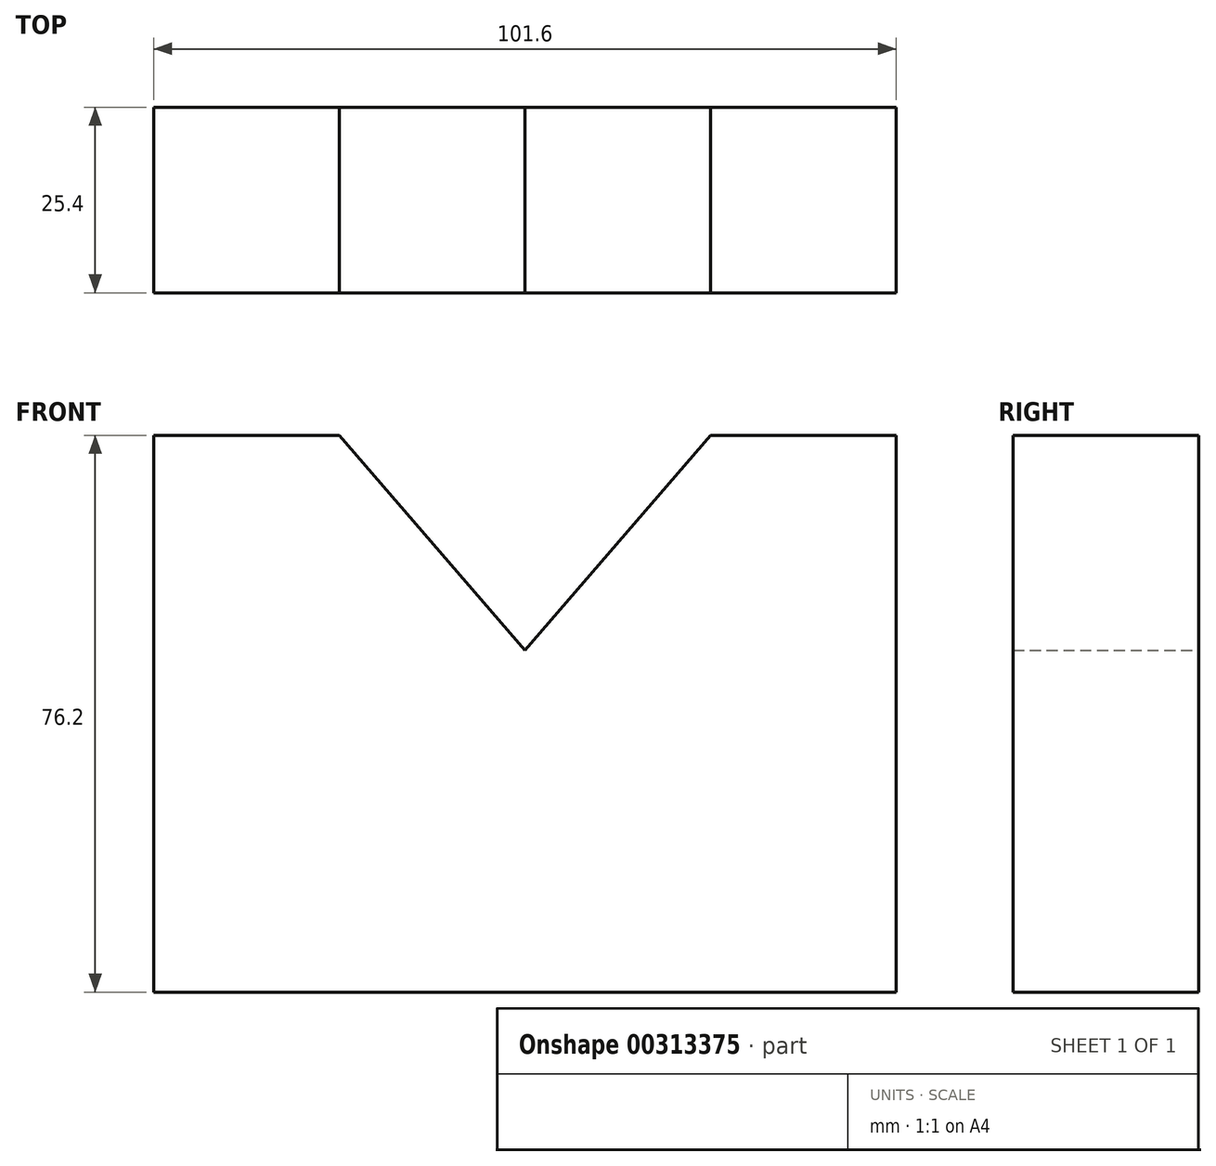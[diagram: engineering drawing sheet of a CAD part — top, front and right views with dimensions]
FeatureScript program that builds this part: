
annotation { "Feature Type Name" : "Feature", "Feature Type Description" : "" }
export const myFeature = defineFeature(function(context is Context, id is Id, definition is map)
    precondition{}
    {
        {
            var Q0;
            Q0=qCreatedBy(makeId("Front.planeOp"),FACE);
            var sketch = newSketch(context, id + "F0", { "sketchPlane" : qUnion([Q0])});
            skLineSegment(sketch, "E0", {"start": v(-43.63, -46.75) * mm, "end": v(57.97, -46.75) * mm});
            skLineSegment(sketch, "E1", {"start": v(-43.63, -46.75) * mm, "end": v(-43.63, 29.45) * mm});
            skLineSegment(sketch, "E2", {"start": v(-43.63, 29.45) * mm, "end": v(-18.23, 29.45) * mm});
            skLineSegment(sketch, "E3", {"start": v(57.97, -46.75) * mm, "end": v(57.97, 29.45) * mm});
            skLineSegment(sketch, "E4", {"start": v(57.97, 29.45) * mm, "end": v(32.57, 29.45) * mm});
            skLineSegment(sketch, "E5", {"start": v(7.17, 0) * mm, "end": v(-18.23, 29.45) * mm});
            skLineSegment(sketch, "E6", {"start": v(32.57, 29.45) * mm, "end": v(7.17, 0) * mm});
            skSolve(sketch);
        }
        {
            var Q0;
            Q0=makeQuery(id+"F0.imprint","IMPRINT",FACE,{"disambiguationData":[TD([[makeQuery(id+"F0.imprint","IMPRINT",EDGE,{"derivedFrom":sQuery(id+"F0.wireOp",EDGE,"E0")}),1.0]])]});
            extrude(context, id + "F1", {"entities" : qUnion([Q0]), "depth" : 25.4 * mm});
        }
    });
